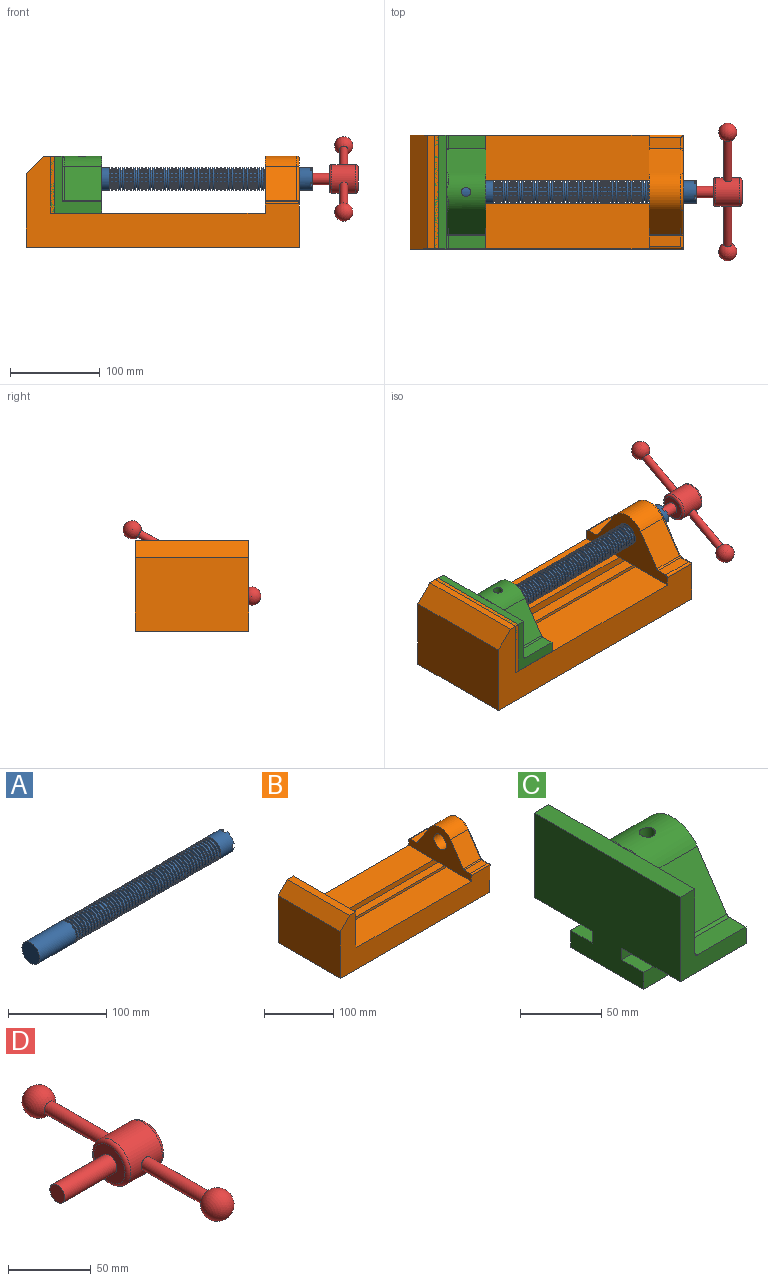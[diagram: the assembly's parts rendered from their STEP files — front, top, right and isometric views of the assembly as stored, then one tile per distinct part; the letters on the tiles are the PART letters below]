
ASSEMBLY  parts=4 mates=3
PART A: 220 faces, bbox 279.4x25.4x25.4 mm
  f0: cylinder r=12.7mm len=25.4mm, axis (-1,0,0), area 1468.2mm2, adj f1,f2,f3,f5,f7,f208,f209,f210
  f1: plane 9.9x9.9mm, normal (1,0,0), area 62.3mm2, adj f0,f4,f213,f216
  f2: plane 9.9x9.9mm, normal (1,0,0), area 62.3mm2, adj f0,f4,f210,f218
  f3: plane 9.9x9.9mm, normal (1,0,0), area 62.3mm2, adj f0,f4,f209,f212
  f4: cylinder r=6.35mm len=25.4mm, axis (1,0,0), area 960.3mm2, adj f1,f2,f3,f5,f6,f208,f209,f210
  f5: plane 9.9x9.9mm, normal (1,0,0), area 62.3mm2, adj f0,f4,f215,f217
  f6: plane 12.7x12.7mm, normal (1,0,0), area 126.7mm2, adj f4
  f7: cone r=12.7mm half-angle=76deg, axis (1,0,0), area 188mm2, adj f0,f9
  f8: cone r=10.16mm half-angle=76deg, axis (-1,0,0), area 188mm2, adj f9,f10
  f9: cylinder r=10.16mm len=20.32mm, axis (1,0,0), area 81.1mm2, adj f7,f8
  f10: cylinder r=12.7mm len=25.4mm, axis (-1,0,0), area 131.7mm2, adj f8,f11
  f11: cone r=12.7mm half-angle=76deg, axis (1,0,0), area 188mm2, adj f10,f13
  f12: cone r=10.16mm half-angle=76deg, axis (-1,0,0), area 188mm2, adj f13,f14
  f13: cylinder r=10.16mm len=20.32mm, axis (1,0,0), area 81.1mm2, adj f11,f12
  f14: cylinder r=12.7mm len=25.4mm, axis (-1,0,0), area 131.7mm2, adj f12,f15
  f15: cone r=12.7mm half-angle=76deg, axis (1,0,0), area 188mm2, adj f14,f17
  f16: cone r=10.16mm half-angle=76deg, axis (-1,0,0), area 188mm2, adj f17,f18
  f17: cylinder r=10.16mm len=20.32mm, axis (1,0,0), area 81.1mm2, adj f15,f16
  f18: cylinder r=12.7mm len=25.4mm, axis (-1,0,0), area 131.7mm2, adj f16,f19
  f19: cone r=12.7mm half-angle=76deg, axis (1,0,0), area 188mm2, adj f18,f21
  f20: cone r=10.16mm half-angle=76deg, axis (-1,0,0), area 188mm2, adj f21,f22
  f21: cylinder r=10.16mm len=20.32mm, axis (1,0,0), area 81.1mm2, adj f19,f20
  f22: cylinder r=12.7mm len=25.4mm, axis (-1,0,0), area 131.7mm2, adj f20,f23
  f23: cone r=12.7mm half-angle=76deg, axis (1,0,0), area 188mm2, adj f22,f25
  f24: cone r=10.16mm half-angle=76deg, axis (-1,0,0), area 188mm2, adj f25,f26
  f25: cylinder r=10.16mm len=20.32mm, axis (1,0,0), area 81.1mm2, adj f23,f24
  f26: cylinder r=12.7mm len=25.4mm, axis (-1,0,0), area 131.7mm2, adj f24,f27
  f27: cone r=12.7mm half-angle=76deg, axis (1,0,0), area 188mm2, adj f26,f29
  f28: cone r=10.16mm half-angle=76deg, axis (-1,0,0), area 188mm2, adj f29,f30
  f29: cylinder r=10.16mm len=20.32mm, axis (1,0,0), area 81.1mm2, adj f27,f28
  f30: cylinder r=12.7mm len=25.4mm, axis (-1,0,0), area 131.7mm2, adj f28,f31
  f31: cone r=12.7mm half-angle=76deg, axis (1,0,0), area 188mm2, adj f30,f33
  f32: cone r=10.16mm half-angle=76deg, axis (-1,0,0), area 188mm2, adj f33,f34
  f33: cylinder r=10.16mm len=20.32mm, axis (1,0,0), area 81.1mm2, adj f31,f32
  f34: cylinder r=12.7mm len=25.4mm, axis (-1,0,0), area 131.7mm2, adj f32,f35
  f35: cone r=12.7mm half-angle=76deg, axis (1,0,0), area 188mm2, adj f34,f37
  f36: cone r=10.16mm half-angle=76deg, axis (-1,0,0), area 188mm2, adj f37,f38
  f37: cylinder r=10.16mm len=20.32mm, axis (1,0,0), area 81.1mm2, adj f35,f36
  f38: cylinder r=12.7mm len=25.4mm, axis (-1,0,0), area 131.7mm2, adj f36,f39
  f39: cone r=12.7mm half-angle=76deg, axis (1,0,0), area 188mm2, adj f38,f41
  f40: cone r=10.16mm half-angle=76deg, axis (-1,0,0), area 188mm2, adj f41,f42
  f41: cylinder r=10.16mm len=20.32mm, axis (1,0,0), area 81.1mm2, adj f39,f40
  f42: cylinder r=12.7mm len=25.4mm, axis (-1,0,0), area 131.7mm2, adj f40,f43
  f43: cone r=12.7mm half-angle=76deg, axis (1,0,0), area 188mm2, adj f42,f45
  f44: cone r=10.16mm half-angle=76deg, axis (-1,0,0), area 188mm2, adj f45,f46
  f45: cylinder r=10.16mm len=20.32mm, axis (1,0,0), area 81.1mm2, adj f43,f44
  f46: cylinder r=12.7mm len=25.4mm, axis (-1,0,0), area 131.7mm2, adj f44,f47
  f47: cone r=12.7mm half-angle=76deg, axis (1,0,0), area 188mm2, adj f46,f49
  f48: cone r=10.16mm half-angle=76deg, axis (-1,0,0), area 188mm2, adj f49,f50
  f49: cylinder r=10.16mm len=20.32mm, axis (1,0,0), area 81.1mm2, adj f47,f48
  f50: cylinder r=12.7mm len=25.4mm, axis (-1,0,0), area 131.7mm2, adj f48,f51
  f51: cone r=12.7mm half-angle=76deg, axis (1,0,0), area 188mm2, adj f50,f53
  f52: cone r=10.16mm half-angle=76deg, axis (-1,0,0), area 188mm2, adj f53,f54
  f53: cylinder r=10.16mm len=20.32mm, axis (1,0,0), area 81.1mm2, adj f51,f52
  f54: cylinder r=12.7mm len=25.4mm, axis (-1,0,0), area 131.7mm2, adj f52,f55
  f55: cone r=12.7mm half-angle=76deg, axis (1,0,0), area 188mm2, adj f54,f57
  f56: cone r=10.16mm half-angle=76deg, axis (-1,0,0), area 188mm2, adj f57,f58
  f57: cylinder r=10.16mm len=20.32mm, axis (1,0,0), area 81.1mm2, adj f55,f56
  f58: cylinder r=12.7mm len=25.4mm, axis (-1,0,0), area 131.7mm2, adj f56,f59
  f59: cone r=12.7mm half-angle=76deg, axis (1,0,0), area 188mm2, adj f58,f61
  f60: cone r=10.16mm half-angle=76deg, axis (-1,0,0), area 188mm2, adj f61,f62
  f61: cylinder r=10.16mm len=20.32mm, axis (1,0,0), area 81.1mm2, adj f59,f60
  f62: cylinder r=12.7mm len=25.4mm, axis (-1,0,0), area 131.7mm2, adj f60,f63
  f63: cone r=12.7mm half-angle=76deg, axis (1,0,0), area 188mm2, adj f62,f65
  f64: cone r=10.16mm half-angle=76deg, axis (-1,0,0), area 188mm2, adj f65,f66
  f65: cylinder r=10.16mm len=20.32mm, axis (1,0,0), area 81.1mm2, adj f63,f64
  f66: cylinder r=12.7mm len=25.4mm, axis (-1,0,0), area 131.7mm2, adj f64,f67
  f67: cone r=12.7mm half-angle=76deg, axis (1,0,0), area 188mm2, adj f66,f69
  f68: cone r=10.16mm half-angle=76deg, axis (-1,0,0), area 188mm2, adj f69,f70
  f69: cylinder r=10.16mm len=20.32mm, axis (1,0,0), area 81.1mm2, adj f67,f68
  f70: cylinder r=12.7mm len=25.4mm, axis (-1,0,0), area 131.7mm2, adj f68,f71
  f71: cone r=12.7mm half-angle=76deg, axis (1,0,0), area 188mm2, adj f70,f73
  f72: cone r=10.16mm half-angle=76deg, axis (-1,0,0), area 188mm2, adj f73,f74
  f73: cylinder r=10.16mm len=20.32mm, axis (1,0,0), area 81.1mm2, adj f71,f72
  f74: cylinder r=12.7mm len=25.4mm, axis (-1,0,0), area 131.7mm2, adj f72,f75
  f75: cone r=12.7mm half-angle=76deg, axis (1,0,0), area 188mm2, adj f74,f77
  f76: cone r=10.16mm half-angle=76deg, axis (-1,0,0), area 188mm2, adj f77,f78
  f77: cylinder r=10.16mm len=20.32mm, axis (1,0,0), area 81.1mm2, adj f75,f76
  f78: cylinder r=12.7mm len=25.4mm, axis (-1,0,0), area 131.7mm2, adj f76,f79
  f79: cone r=12.7mm half-angle=76deg, axis (1,0,0), area 188mm2, adj f78,f81
  f80: cone r=10.16mm half-angle=76deg, axis (-1,0,0), area 188mm2, adj f81,f82
  f81: cylinder r=10.16mm len=20.32mm, axis (1,0,0), area 81.1mm2, adj f79,f80
  f82: cylinder r=12.7mm len=25.4mm, axis (-1,0,0), area 131.7mm2, adj f80,f83
  f83: cone r=12.7mm half-angle=76deg, axis (1,0,0), area 188mm2, adj f82,f85
  f84: cone r=10.16mm half-angle=76deg, axis (-1,0,0), area 188mm2, adj f85,f86
  f85: cylinder r=10.16mm len=20.32mm, axis (1,0,0), area 81.1mm2, adj f83,f84
  f86: cylinder r=12.7mm len=25.4mm, axis (-1,0,0), area 131.7mm2, adj f84,f87
  f87: cone r=12.7mm half-angle=76deg, axis (1,0,0), area 188mm2, adj f86,f89
  f88: cone r=10.16mm half-angle=76deg, axis (-1,0,0), area 188mm2, adj f89,f90
  f89: cylinder r=10.16mm len=20.32mm, axis (1,0,0), area 81.1mm2, adj f87,f88
  f90: cylinder r=12.7mm len=25.4mm, axis (-1,0,0), area 131.7mm2, adj f88,f91
  f91: cone r=12.7mm half-angle=76deg, axis (1,0,0), area 188mm2, adj f90,f93
  f92: cone r=10.16mm half-angle=76deg, axis (-1,0,0), area 188mm2, adj f93,f94
  f93: cylinder r=10.16mm len=20.32mm, axis (1,0,0), area 81.1mm2, adj f91,f92
  f94: cylinder r=12.7mm len=25.4mm, axis (-1,0,0), area 131.7mm2, adj f92,f95
  f95: cone r=12.7mm half-angle=76deg, axis (1,0,0), area 188mm2, adj f94,f97
  f96: cone r=10.16mm half-angle=76deg, axis (-1,0,0), area 188mm2, adj f97,f98
  f97: cylinder r=10.16mm len=20.32mm, axis (1,0,0), area 81.1mm2, adj f95,f96
  f98: cylinder r=12.7mm len=25.4mm, axis (-1,0,0), area 131.7mm2, adj f96,f99
  f99: cone r=12.7mm half-angle=76deg, axis (1,0,0), area 188mm2, adj f98,f101
  f100: cone r=10.16mm half-angle=76deg, axis (-1,0,0), area 188mm2, adj f101,f102
  f101: cylinder r=10.16mm len=20.32mm, axis (1,0,0), area 81.1mm2, adj f99,f100
  f102: cylinder r=12.7mm len=25.4mm, axis (-1,0,0), area 131.7mm2, adj f100,f103
  f103: cone r=12.7mm half-angle=76deg, axis (1,0,0), area 188mm2, adj f102,f105
  f104: cone r=10.16mm half-angle=76deg, axis (-1,0,0), area 188mm2, adj f105,f106
  f105: cylinder r=10.16mm len=20.32mm, axis (1,0,0), area 81.1mm2, adj f103,f104
  f106: cylinder r=12.7mm len=25.4mm, axis (-1,0,0), area 131.7mm2, adj f104,f107
  f107: cone r=12.7mm half-angle=76deg, axis (1,0,0), area 188mm2, adj f106,f109
  f108: cone r=10.16mm half-angle=76deg, axis (-1,0,0), area 188mm2, adj f109,f110
  f109: cylinder r=10.16mm len=20.32mm, axis (1,0,0), area 81.1mm2, adj f107,f108
  f110: cylinder r=12.7mm len=25.4mm, axis (-1,0,0), area 131.7mm2, adj f108,f111
  f111: cone r=12.7mm half-angle=76deg, axis (1,0,0), area 188mm2, adj f110,f113
  f112: cone r=10.16mm half-angle=76deg, axis (-1,0,0), area 188mm2, adj f113,f114
  f113: cylinder r=10.16mm len=20.32mm, axis (1,0,0), area 81.1mm2, adj f111,f112
  f114: cylinder r=12.7mm len=25.4mm, axis (-1,0,0), area 131.7mm2, adj f112,f115
  f115: cone r=12.7mm half-angle=76deg, axis (1,0,0), area 188mm2, adj f114,f117
  f116: cone r=10.16mm half-angle=76deg, axis (-1,0,0), area 188mm2, adj f117,f118
  f117: cylinder r=10.16mm len=20.32mm, axis (1,0,0), area 81.1mm2, adj f115,f116
  f118: cylinder r=12.7mm len=25.4mm, axis (-1,0,0), area 131.7mm2, adj f116,f119
  f119: cone r=12.7mm half-angle=76deg, axis (1,0,0), area 188mm2, adj f118,f121
  f120: cone r=10.16mm half-angle=76deg, axis (-1,0,0), area 188mm2, adj f121,f122
  f121: cylinder r=10.16mm len=20.32mm, axis (1,0,0), area 81.1mm2, adj f119,f120
  f122: cylinder r=12.7mm len=25.4mm, axis (-1,0,0), area 131.7mm2, adj f120,f123
  f123: cone r=12.7mm half-angle=76deg, axis (1,0,0), area 188mm2, adj f122,f125
  f124: cone r=10.16mm half-angle=76deg, axis (-1,0,0), area 188mm2, adj f125,f126
  f125: cylinder r=10.16mm len=20.32mm, axis (1,0,0), area 81.1mm2, adj f123,f124
  f126: cylinder r=12.7mm len=25.4mm, axis (-1,0,0), area 131.7mm2, adj f124,f127
  f127: cone r=12.7mm half-angle=76deg, axis (1,0,0), area 188mm2, adj f126,f129
  f128: cone r=10.16mm half-angle=76deg, axis (-1,0,0), area 188mm2, adj f129,f130
  f129: cylinder r=10.16mm len=20.32mm, axis (1,0,0), area 81.1mm2, adj f127,f128
  f130: cylinder r=12.7mm len=25.4mm, axis (-1,0,0), area 131.7mm2, adj f128,f131
  f131: cone r=12.7mm half-angle=76deg, axis (1,0,0), area 188mm2, adj f130,f133
  f132: cone r=10.16mm half-angle=76deg, axis (-1,0,0), area 188mm2, adj f133,f134
  f133: cylinder r=10.16mm len=20.32mm, axis (1,0,0), area 81.1mm2, adj f131,f132
  f134: cylinder r=12.7mm len=25.4mm, axis (-1,0,0), area 131.7mm2, adj f132,f135
  f135: cone r=12.7mm half-angle=76deg, axis (1,0,0), area 188mm2, adj f134,f137
  f136: cone r=10.16mm half-angle=76deg, axis (-1,0,0), area 188mm2, adj f137,f138
  f137: cylinder r=10.16mm len=20.32mm, axis (1,0,0), area 81.1mm2, adj f135,f136
  f138: cylinder r=12.7mm len=25.4mm, axis (-1,0,0), area 131.7mm2, adj f136,f139
  f139: cone r=12.7mm half-angle=76deg, axis (1,0,0), area 188mm2, adj f138,f141
  f140: cone r=10.16mm half-angle=76deg, axis (-1,0,0), area 188mm2, adj f141,f142
  f141: cylinder r=10.16mm len=20.32mm, axis (1,0,0), area 81.1mm2, adj f139,f140
  f142: cylinder r=12.7mm len=25.4mm, axis (-1,0,0), area 131.7mm2, adj f140,f143
  f143: cone r=12.7mm half-angle=76deg, axis (1,0,0), area 188mm2, adj f142,f145
  f144: cone r=10.16mm half-angle=76deg, axis (-1,0,0), area 188mm2, adj f145,f146
  f145: cylinder r=10.16mm len=20.32mm, axis (1,0,0), area 81.1mm2, adj f143,f144
  f146: cylinder r=12.7mm len=25.4mm, axis (-1,0,0), area 131.7mm2, adj f144,f147
  f147: cone r=12.7mm half-angle=76deg, axis (1,0,0), area 188mm2, adj f146,f149
  f148: cone r=10.16mm half-angle=76deg, axis (-1,0,0), area 188mm2, adj f149,f150
  f149: cylinder r=10.16mm len=20.32mm, axis (1,0,0), area 81.1mm2, adj f147,f148
  f150: cylinder r=12.7mm len=25.4mm, axis (-1,0,0), area 131.7mm2, adj f148,f151
  f151: cone r=12.7mm half-angle=76deg, axis (1,0,0), area 188mm2, adj f150,f153
  f152: cone r=10.16mm half-angle=76deg, axis (-1,0,0), area 188mm2, adj f153,f154
  f153: cylinder r=10.16mm len=20.32mm, axis (1,0,0), area 81.1mm2, adj f151,f152
  f154: cylinder r=12.7mm len=25.4mm, axis (-1,0,0), area 131.7mm2, adj f152,f155
  f155: cone r=12.7mm half-angle=76deg, axis (1,0,0), area 188mm2, adj f154,f157
  f156: cone r=10.16mm half-angle=76deg, axis (-1,0,0), area 188mm2, adj f157,f158
  f157: cylinder r=10.16mm len=20.32mm, axis (1,0,0), area 81.1mm2, adj f155,f156
  f158: cylinder r=12.7mm len=25.4mm, axis (-1,0,0), area 131.7mm2, adj f156,f159
  f159: cone r=12.7mm half-angle=76deg, axis (1,0,0), area 188mm2, adj f158,f161
  f160: cone r=10.16mm half-angle=76deg, axis (-1,0,0), area 188mm2, adj f161,f162
  f161: cylinder r=10.16mm len=20.32mm, axis (1,0,0), area 81.1mm2, adj f159,f160
  f162: cylinder r=12.7mm len=25.4mm, axis (-1,0,0), area 131.7mm2, adj f160,f163
  f163: cone r=12.7mm half-angle=76deg, axis (1,0,0), area 188mm2, adj f162,f165
  f164: cone r=10.16mm half-angle=76deg, axis (-1,0,0), area 188mm2, adj f165,f166
  f165: cylinder r=10.16mm len=20.32mm, axis (1,0,0), area 81.1mm2, adj f163,f164
  f166: cylinder r=12.7mm len=25.4mm, axis (-1,0,0), area 131.7mm2, adj f164,f167
  f167: cone r=12.7mm half-angle=76deg, axis (1,0,0), area 188mm2, adj f166,f169
  f168: cone r=10.16mm half-angle=76deg, axis (-1,0,0), area 188mm2, adj f169,f170
  f169: cylinder r=10.16mm len=20.32mm, axis (1,0,0), area 81.1mm2, adj f167,f168
  f170: cylinder r=12.7mm len=25.4mm, axis (-1,0,0), area 131.7mm2, adj f168,f171
  f171: cone r=12.7mm half-angle=76deg, axis (1,0,0), area 188mm2, adj f170,f173
  f172: cone r=10.16mm half-angle=76deg, axis (-1,0,0), area 188mm2, adj f173,f174
  f173: cylinder r=10.16mm len=20.32mm, axis (1,0,0), area 81.1mm2, adj f171,f172
  f174: cylinder r=12.7mm len=25.4mm, axis (-1,0,0), area 131.7mm2, adj f172,f175
  f175: cone r=12.7mm half-angle=76deg, axis (1,0,0), area 188mm2, adj f174,f177
  f176: cone r=10.16mm half-angle=76deg, axis (-1,0,0), area 188mm2, adj f177,f178
  f177: cylinder r=10.16mm len=20.32mm, axis (1,0,0), area 81.1mm2, adj f175,f176
  f178: cylinder r=12.7mm len=25.4mm, axis (-1,0,0), area 131.7mm2, adj f176,f179
  f179: cone r=12.7mm half-angle=76deg, axis (1,0,0), area 188mm2, adj f178,f181
  f180: cone r=10.16mm half-angle=76deg, axis (-1,0,0), area 188mm2, adj f181,f182
  f181: cylinder r=10.16mm len=20.32mm, axis (1,0,0), area 81.1mm2, adj f179,f180
  f182: cylinder r=12.7mm len=25.4mm, axis (-1,0,0), area 131.7mm2, adj f180,f183
  f183: cone r=12.7mm half-angle=76deg, axis (1,0,0), area 188mm2, adj f182,f185
  f184: cone r=10.16mm half-angle=76deg, axis (-1,0,0), area 188mm2, adj f185,f186
  f185: cylinder r=10.16mm len=20.32mm, axis (1,0,0), area 81.1mm2, adj f183,f184
  f186: cylinder r=12.7mm len=25.4mm, axis (-1,0,0), area 131.7mm2, adj f184,f187
  f187: cone r=12.7mm half-angle=76deg, axis (1,0,0), area 188mm2, adj f186,f189
  f188: cone r=10.16mm half-angle=76deg, axis (-1,0,0), area 188mm2, adj f189,f190
  f189: cylinder r=10.16mm len=20.32mm, axis (1,0,0), area 81.1mm2, adj f187,f188
  f190: cylinder r=12.7mm len=25.4mm, axis (-1,0,0), area 131.7mm2, adj f188,f191
  f191: cone r=12.7mm half-angle=76deg, axis (1,0,0), area 188mm2, adj f190,f193
  f192: cone r=10.16mm half-angle=76deg, axis (-1,0,0), area 188mm2, adj f193,f194
  f193: cylinder r=10.16mm len=20.32mm, axis (1,0,0), area 81.1mm2, adj f191,f192
  f194: cylinder r=12.7mm len=25.4mm, axis (-1,0,0), area 131.7mm2, adj f192,f195
  f195: cone r=12.7mm half-angle=76deg, axis (1,0,0), area 188mm2, adj f194,f197
  f196: cone r=10.16mm half-angle=76deg, axis (-1,0,0), area 188mm2, adj f197,f198
  f197: cylinder r=10.16mm len=20.32mm, axis (1,0,0), area 81.1mm2, adj f195,f196
  f198: cylinder r=12.7mm len=25.4mm, axis (-1,0,0), area 131.7mm2, adj f196,f199
  f199: cone r=12.7mm half-angle=76deg, axis (1,0,0), area 188mm2, adj f198,f201
  f200: cone r=10.16mm half-angle=76deg, axis (-1,0,0), area 188mm2, adj f201,f202
  f201: cylinder r=10.16mm len=20.32mm, axis (1,0,0), area 81.1mm2, adj f199,f200
  f202: cylinder r=12.7mm len=25.4mm, axis (-1,0,0), area 131.7mm2, adj f200,f203
  f203: cone r=12.7mm half-angle=76deg, axis (1,0,0), area 188mm2, adj f202,f205
  f204: cone r=10.16mm half-angle=76deg, axis (-1,0,0), area 188mm2, adj f205,f207
  f205: cylinder r=10.16mm len=20.32mm, axis (1,0,0), area 81.1mm2, adj f203,f204
  f206: plane 25.4x25.4mm, normal (-1,0,0), area 506.7mm2, adj f207
  f207: cylinder r=12.7mm len=52.45mm, axis (-1,0,0), area 4185.4mm2, adj f204,f206
  f208: plane 6.88x5.08mm, normal (1,0,0), area 32.7mm2, adj f0,f4,f209,f210
  f209: plane 6.62x2.54mm, normal (0,-1,0), area 16.8mm2, adj f0,f3,f4,f208
  f210: plane 6.62x2.54mm, normal (0,1,0), area 16.8mm2, adj f0,f2,f4,f208
  f211: plane 6.88x5.08mm, normal (1,0,0), area 32.7mm2, adj f0,f4,f212,f213
  f212: plane 6.62x2.54mm, normal (0,0,1), area 16.8mm2, adj f0,f3,f4,f211
  f213: plane 6.62x2.54mm, normal (0,0,-1), area 16.8mm2, adj f0,f1,f4,f211
  f214: plane 6.88x5.08mm, normal (1,0,0), area 32.7mm2, adj f0,f4,f215,f216
  f215: plane 6.62x2.54mm, normal (0,1,0), area 16.8mm2, adj f0,f4,f5,f214
  f216: plane 6.62x2.54mm, normal (0,-1,0), area 16.8mm2, adj f0,f1,f4,f214
  f217: plane 6.62x2.54mm, normal (0,0,-1), area 16.8mm2, adj f0,f4,f5,f219
  f218: plane 6.62x2.54mm, normal (0,0,1), area 16.8mm2, adj f0,f2,f4,f219
  f219: plane 6.88x5.08mm, normal (1,0,0), area 32.7mm2, adj f0,f4,f217,f218
PART B: 39 faces, bbox 304.8x127x103.7 mm
  f0: plane 234.95x50.8mm, normal (0,0,1), area 11935.5mm2, adj f3,f8,f16,f26
  f1: plane 127x99.06mm, normal (1,0,0), area 7097.5mm2, adj f7,f8,f9,f14,f17,f18,f19,f20
  f2: plane 234.95x50.8mm, normal (0,0,1), area 11935.5mm2, adj f3,f9,f16,f27
  f3: plane 127x101.6mm, normal (1,0,0), area 9516.1mm2, adj f0,f2,f4,f7,f8,f9,f18,f19
  f4: plane 127x12.7mm, normal (0,0,1), area 1612.9mm2, adj f3,f5,f8,f9
  f5: plane 127x19.05mm, normal (-0.71,0,0.71), area 3421.5mm2, adj f4,f6,f8,f9
  f6: plane 127x82.55mm, normal (-1,0,0), area 10483.8mm2, adj f5,f7,f8,f9
  f7: plane 304.8x127mm, normal (0,0,-1), area 31774.1mm2, adj f1,f3,f6,f8,f9,f21,f22
  f8: plane 304.8x101.6mm, normal (0,-1,0), area 13834.6mm2, adj f0,f1,f3,f4,f5,f6,f7,f16
  f9: plane 304.8x101.6mm, normal (0,1,0), area 13834.6mm2, adj f1,f2,f3,f4,f5,f6,f7,f16
  f10: plane 35.56x11.98mm, normal (0,0,1), area 426mm2, adj f16,f28,f29,f30
  f11: plane 38.43x35.56mm, normal (0,0.83,0.56), area 1645.4mm2, adj f12,f16,f29,f32
  f12: cylinder r=25.4mm len=42.19mm, axis (1,0,0), area 1770.2mm2, adj f11,f13,f16,f33
  f13: plane 38.43x35.56mm, normal (0,-0.83,0.56), area 1645.4mm2, adj f12,f16,f34,f35
  f14: cylinder r=12.7mm len=38.1mm, axis (1,0,0), area 3040.2mm2, adj f1,f16
  f15: plane 35.56x11.98mm, normal (0,0,1), area 426mm2, adj f16,f34,f36,f38
  f16: plane 127x63.5mm, normal (-1,0,0), area 4155.5mm2, adj f0,f2,f8,f9,f10,f11,f12,f13
  f17: plane 38.1x25.4mm, normal (0,0,-1), area 967.7mm2, adj f1,f16,f26,f27
  f18: plane 273.05x19.05mm, normal (0,0,-1), area 5201.6mm2, adj f1,f3,f19,f26
  f19: plane 273.05x12.7mm, normal (0,1,0), area 3467.7mm2, adj f1,f3,f18,f20
  f20: plane 273.05x19.05mm, normal (0,0,1), area 5201.6mm2, adj f1,f3,f19,f21
  f21: plane 273.05x16.51mm, normal (0,1,0), area 4508.1mm2, adj f1,f3,f7,f20
  f22: plane 273.05x16.51mm, normal (0,-1,0), area 4508.1mm2, adj f1,f3,f7,f23
  f23: plane 273.05x19.05mm, normal (0,0,1), area 5201.6mm2, adj f1,f3,f22,f24
  f24: plane 273.05x12.7mm, normal (0,-1,0), area 3467.7mm2, adj f1,f3,f23,f25
  f25: plane 273.05x19.05mm, normal (0,0,-1), area 5201.6mm2, adj f1,f3,f24,f27
  f26: plane 273.05x8.89mm, normal (0,1,0), area 2427.4mm2, adj f0,f1,f3,f17,f18
  f27: plane 273.05x8.89mm, normal (0,-1,0), area 2427.4mm2, adj f1,f2,f3,f17,f25
  f28: cylinder r=2.54mm len=38.1mm, axis (1,0,0), area 148.3mm2, adj f9,f10,f16,f30
  f29: cylinder r=2.54mm len=35.56mm, axis (-1,0,0), area 88.5mm2, adj f10,f11,f16,f31
  f30: cylinder r=2.54mm len=14.52mm, axis (0,1,0), area 54.3mm2, adj f1,f10,f28,f31
  f31: torus R=5.08mm, axis (-1,0,0), area 13.5mm2, adj f1,f29,f30,f32
  f32: cylinder r=2.54mm len=39.84mm, axis (0,0.56,-0.83), area 184.6mm2, adj f1,f11,f31,f33
  f33: torus R=22.86mm, axis (-1,0,0), area 191.4mm2, adj f1,f12,f32,f35
  f34: cylinder r=2.54mm len=35.56mm, axis (-1,0,0), area 88.5mm2, adj f13,f15,f16,f37
  f35: cylinder r=2.54mm len=39.84mm, axis (0,0.56,0.83), area 184.6mm2, adj f1,f13,f33,f37
  f36: cylinder r=2.54mm len=38.1mm, axis (-1,0,0), area 148.3mm2, adj f8,f15,f16,f38
  f37: torus R=5.08mm, axis (-1,0,0), area 13.5mm2, adj f1,f34,f35,f38
  f38: cylinder r=2.54mm len=14.52mm, axis (0,1,0), area 54.3mm2, adj f1,f15,f36,f37
PART C: 36 faces, bbox 57.2x127x89 mm
  f0: plane 57.15x50.8mm, normal (0,0,-1), area 2903.2mm2, adj f6,f9,f10,f23
  f1: cylinder r=12.7mm len=44.45mm, axis (1,0,0), area 3464.3mm2, adj f6,f15,f16
  f2: plane 41.91x14.52mm, normal (0,0,1), area 608.5mm2, adj f6,f11,f24,f25
  f3: plane 51.86x48.26mm, normal (1,0,0), area 1495.7mm2, adj f8,f10,f31,f33,f35
  f4: plane 51.86x48.26mm, normal (1,0,0), area 1495.7mm2, adj f8,f11,f24,f28,f29
  f5: plane 57.15x50.8mm, normal (0,0,-1), area 2903.2mm2, adj f6,f9,f11,f22
  f6: plane 127x85.09mm, normal (1,0,0), area 5190.6mm2, adj f0,f1,f2,f5,f7,f10,f11,f12
  f7: plane 41.91x14.52mm, normal (0,0,1), area 608.5mm2, adj f6,f10,f30,f31
  f8: plane 127x12.7mm, normal (0,0,1), area 1612.9mm2, adj f3,f4,f9,f10,f11,f26,f34
  f9: plane 127x85.09mm, normal (-1,0,0), area 9096.8mm2, adj f0,f5,f8,f10,f11,f17,f18,f19
  f10: plane 63.5x57.15mm, normal (0,-1,0), area 1372.3mm2, adj f0,f3,f6,f7,f8,f9,f31
  f11: plane 63.5x57.15mm, normal (0,1,0), area 1372.3mm2, adj f2,f4,f5,f6,f8,f9,f24
  f12: plane 41.91x38.43mm, normal (0,-0.83,0.56), area 1939.2mm2, adj f6,f13,f30,f33
  f13: cylinder r=25.4mm len=44.45mm, axis (1,0,0), area 2026.5mm2, adj f6,f12,f14,f16,f26,f28,f34,f35
  f14: plane 41.91x38.43mm, normal (0,0.83,0.56), area 1939.2mm2, adj f6,f13,f25,f29
  f15: plane 25.4x25.4mm, normal (1,0,0), area 506.7mm2, adj f1
  f16: cylinder r=5.08mm len=13.76mm, axis (0,0,1), area 414mm2, adj f1,f13
  f17: plane 57.15x19.05mm, normal (0,0,1), area 1088.7mm2, adj f6,f9,f18,f23
  f18: plane 57.15x12.7mm, normal (0,-1,0), area 725.8mm2, adj f6,f9,f17,f19
  f19: plane 63.5x57.15mm, normal (0,0,-1), area 3629mm2, adj f6,f9,f18,f20
  f20: plane 57.15x12.7mm, normal (0,1,0), area 725.8mm2, adj f6,f9,f19,f21
  f21: plane 57.15x19.05mm, normal (0,0,1), area 1088.7mm2, adj f6,f9,f20,f22
  f22: plane 57.15x8.89mm, normal (0,1,0), area 508.1mm2, adj f5,f6,f9,f21
  f23: plane 57.15x8.89mm, normal (0,-1,0), area 508.1mm2, adj f0,f6,f9,f17
  f24: cylinder r=2.54mm len=14.52mm, axis (0,-1,0), area 57.9mm2, adj f2,f4,f11,f27
  f25: cylinder r=2.54mm len=41.91mm, axis (1,0,0), area 104.3mm2, adj f2,f6,f14,f27
  f26: bspline ~12.24x2.8mm, area 20.9mm2, adj f8,f13,f28
  f27: sphere r=2.54mm, area 6.3mm2, adj f24,f25,f29
  f28: torus R=27.94mm, axis (1,0,0), area 57.8mm2, adj f4,f13,f26,f29
  f29: cylinder r=2.54mm len=39.84mm, axis (0,-0.56,0.83), area 184.6mm2, adj f4,f14,f27,f28
  f30: cylinder r=2.54mm len=41.91mm, axis (1,0,0), area 104.3mm2, adj f6,f7,f12,f32
  f31: cylinder r=2.54mm len=14.52mm, axis (0,-1,0), area 57.9mm2, adj f3,f7,f10,f32
  f32: sphere r=2.54mm, area 6.3mm2, adj f30,f31,f33
  f33: cylinder r=2.54mm len=39.84mm, axis (0,-0.56,-0.83), area 184.6mm2, adj f3,f12,f32,f35
  f34: bspline ~12.24x2.8mm, area 20.9mm2, adj f8,f13,f35
  f35: torus R=27.94mm, axis (1,0,0), area 57.8mm2, adj f3,f13,f33,f34
PART D: 11 faces, bbox 76.2x172.7x34.4 mm
  f0: sphere r=10.16mm, area 1231.8mm2, adj f1
  f1: cylinder r=4.45mm len=51.82mm, axis (0,1,0), area 1438.5mm2, adj f0,f4
  f2: sphere r=10.16mm, area 1231.8mm2, adj f3
  f3: cylinder r=4.45mm len=51.82mm, axis (0,1,0), area 1438.5mm2, adj f2,f4
  f4: cylinder r=15.88mm len=31.75mm, axis (-1,0,0), area 2534.7mm2, adj f1,f3,f9,f10
  f5: cylinder r=6.35mm len=44.45mm, axis (-1,0,0), area 1773.5mm2, adj f6,f8
  f6: plane 12.7x12.7mm, normal (-1,0,0), area 126.7mm2, adj f5
  f7: plane 26.67x26.67mm, normal (1,0,0), area 558.6mm2, adj f10
  f8: plane 26.67x26.67mm, normal (-1,0,0), area 432mm2, adj f5,f9
  f9: torus R=13.33mm, axis (1,0,0), area 374.8mm2, adj f4,f8
  f10: torus R=13.33mm, axis (1,0,0), area 374.8mm2, adj f4,f7
PLACE A rot(axis=(-1,0,0),151deg) t=(-4.25,-36.95,142.84)mm
PLACE B at identity fixed
PLACE C t=(-4.25,0,0)mm
PLACE D rot(axis=(-1,0,0),151deg) t=(-4.25,-36.95,142.84)mm
MATE fastened A.f4 <-> D.f5  axis (1,0,0) through (-10.6,0,76.2)mm
MATE revolute C.f28 <-> A.f7  axis (1,0,0) through (-264.6,0,76.2)mm
MATE slider B.f3 <-> C.f9  axis (-1,0,0) through (-273.05,-63.5,38.1)mm
